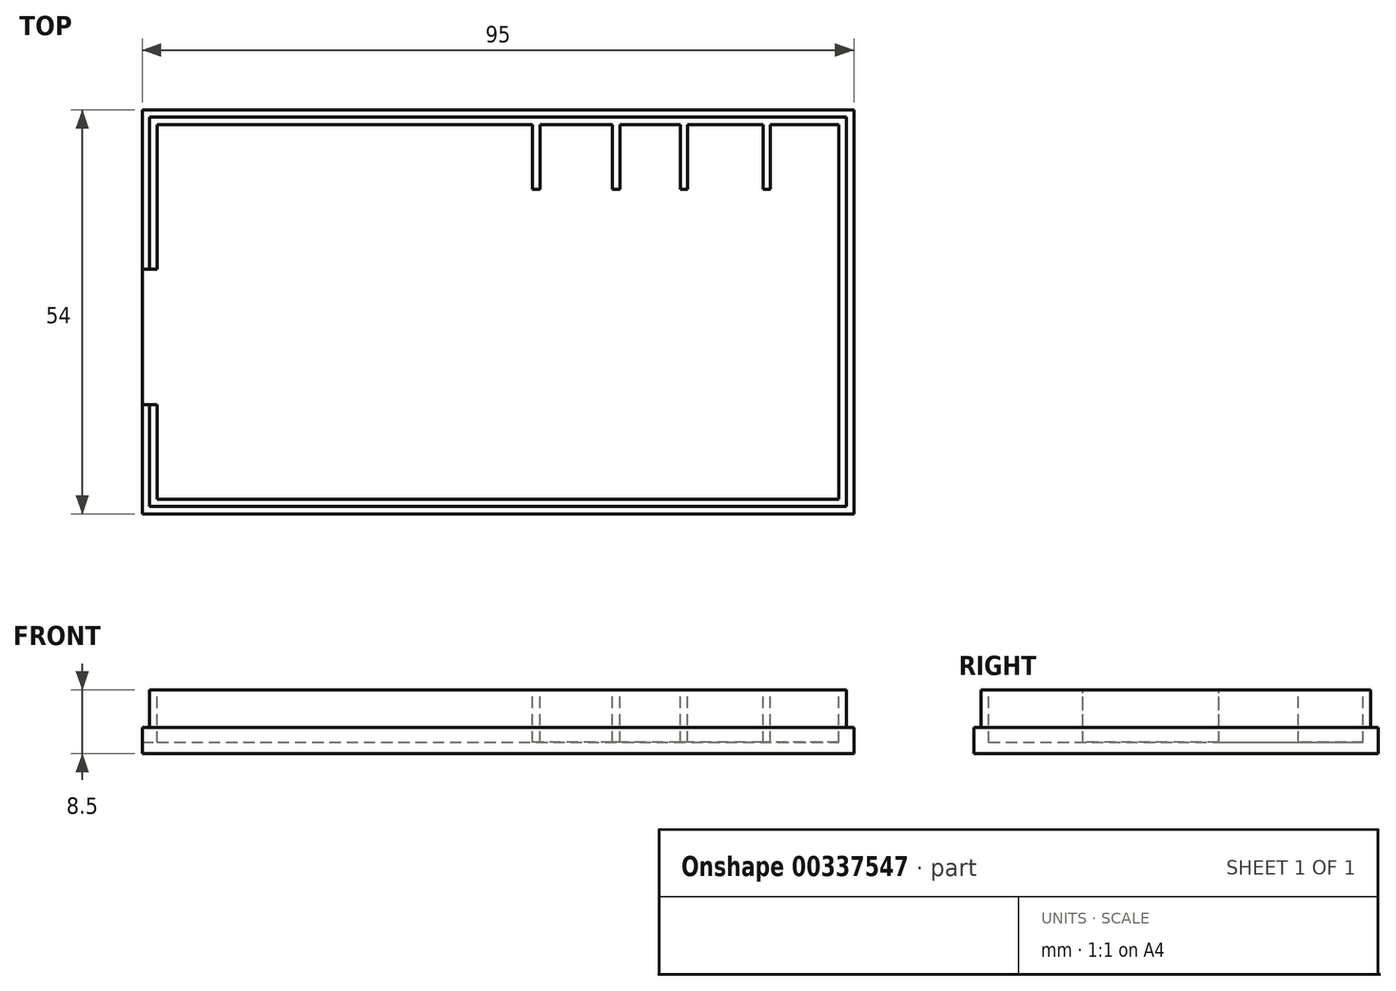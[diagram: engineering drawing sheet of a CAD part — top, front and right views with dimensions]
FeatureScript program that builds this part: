
annotation { "Feature Type Name" : "Feature", "Feature Type Description" : "" }
export const myFeature = defineFeature(function(context is Context, id is Id, definition is map)
    precondition{}
    {
        {
            var Q0;
            Q0=qCreatedBy(makeId("Top.planeOp"),FACE);
            var sketch = newSketch(context, id + "F0", { "sketchPlane" : qUnion([Q0])});
            skLineSegment(sketch, "E0.bottom", {"start": v(-47.5, 27) * mm, "end": v(47.5, 27) * mm});
            skLineSegment(sketch, "E0.top", {"start": v(-47.5, -27) * mm, "end": v(47.5, -27) * mm});
            skLineSegment(sketch, "E0.left", {"start": v(-47.5, 27) * mm, "end": v(-47.5, -27) * mm});
            skLineSegment(sketch, "E0.right", {"start": v(47.5, 27) * mm, "end": v(47.5, -27) * mm});
            skSolve(sketch);
        }
        {
            var Q0;
            Q0 = qSketchRegion(id + "F0", true);
            extrude(context, id + "F1", {"entities" : qUnion([Q0]), "depth" : 8.5 * mm});
        }
        {
            var Q0;
            Q0=makeQuery(id+"F1.opExtrude","CAP_FACE",FACE,{"disambiguationData":[OSD([sQuery(id+"F0.wireOp",EDGE,"E0.bottom"),sQuery(id+"F0.wireOp",EDGE,"E0.top"),sQuery(id+"F0.wireOp",EDGE,"E0.left"),sQuery(id+"F0.wireOp",EDGE,"E0.right")])],"isStart":false});
            var sketch = newSketch(context, id + "F2", { "sketchPlane" : qUnion([Q0])});
            skLineSegment(sketch, "E1.bottom", {"start": v(-45.5, -25) * mm, "end": v(45.5, -25) * mm});
            skLineSegment(sketch, "E1.left", {"start": v(-45.5, -25) * mm, "end": v(-45.5, 25) * mm});
            skLineSegment(sketch, "E1.right", {"start": v(45.5, -25) * mm, "end": v(45.5, 25) * mm});
            skLineSegment(sketch, "E2", {"start": v(36.37, 25) * mm, "end": v(36.37, 16.35) * mm});
            skLineSegment(sketch, "E3", {"start": v(36.37, 16.35) * mm, "end": v(35.37, 16.35) * mm});
            skLineSegment(sketch, "E4", {"start": v(35.37, 16.35) * mm, "end": v(35.37, 25) * mm});
            skLineSegment(sketch, "E5", {"start": v(45.5, 25) * mm, "end": v(36.37, 25) * mm});
            skLineSegment(sketch, "E6", {"start": v(35.37, 25) * mm, "end": v(25.32, 25) * mm});
            skLineSegment(sketch, "E7", {"start": v(25.32, 25) * mm, "end": v(25.32, 16.35) * mm});
            skLineSegment(sketch, "E8", {"start": v(25.32, 16.35) * mm, "end": v(24.32, 16.35) * mm});
            skLineSegment(sketch, "E9", {"start": v(24.32, 16.35) * mm, "end": v(24.32, 25) * mm});
            skLineSegment(sketch, "E10", {"start": v(24.32, 25) * mm, "end": v(16.26, 25) * mm});
            skLineSegment(sketch, "E11", {"start": v(16.26, 25) * mm, "end": v(16.26, 16.35) * mm});
            skLineSegment(sketch, "E12", {"start": v(16.26, 16.35) * mm, "end": v(15.26, 16.35) * mm});
            skLineSegment(sketch, "E13", {"start": v(15.26, 16.35) * mm, "end": v(15.26, 25) * mm});
            skLineSegment(sketch, "E14", {"start": v(15.26, 25) * mm, "end": v(5.62, 25) * mm});
            skLineSegment(sketch, "E15", {"start": v(5.62, 25) * mm, "end": v(5.62, 16.35) * mm});
            skLineSegment(sketch, "E16", {"start": v(5.62, 16.35) * mm, "end": v(4.62, 16.35) * mm});
            skLineSegment(sketch, "E17", {"start": v(4.62, 16.35) * mm, "end": v(4.62, 25) * mm});
            skLineSegment(sketch, "E18", {"start": v(-45.5, 25) * mm, "end": v(4.62, 25) * mm});
            skSolve(sketch);
        }
        {
            var Q0;
            Q0 = qSketchRegion(id + "F2", true);
            extrude(context, id + "F3", {"entities" : qUnion([Q0]), "operationType" : NewBodyOperationType.REMOVE, "oppositeDirection" : true, "depth" : 7 * mm});
        }
        {
            var Q0;
            Q0=makeQuery(id+"F1.opExtrude","CAP_FACE",FACE,{"disambiguationData":[OSD([sQuery(id+"F0.wireOp",EDGE,"E0.bottom"),sQuery(id+"F0.wireOp",EDGE,"E0.top"),sQuery(id+"F0.wireOp",EDGE,"E0.left"),sQuery(id+"F0.wireOp",EDGE,"E0.right")])],"isStart":false});
            var sketch = newSketch(context, id + "F4", { "sketchPlane" : qUnion([Q0])});
            skLineSegment(sketch, "E19.bottom", {"start": v(-47.5, -12.4) * mm, "end": v(-45.5, -12.4) * mm});
            skLineSegment(sketch, "E19.top", {"start": v(-47.5, 5.7) * mm, "end": v(-45.5, 5.7) * mm});
            skLineSegment(sketch, "E19.left", {"start": v(-47.5, -12.4) * mm, "end": v(-47.5, 5.7) * mm});
            skLineSegment(sketch, "E19.right", {"start": v(-45.5, -12.4) * mm, "end": v(-45.5, 5.7) * mm});
            skSolve(sketch);
        }
        {
            var Q0;
            Q0 = qSketchRegion(id + "F4", true);
            extrude(context, id + "F5", {"entities" : qUnion([Q0]), "operationType" : NewBodyOperationType.REMOVE, "oppositeDirection" : true, "depth" : 7 * mm});
        }
        {
            var Q0;
            Q0=makeQuery(id+"F1.opExtrude","CAP_FACE",FACE,{"disambiguationData":[OSD([sQuery(id+"F0.wireOp",EDGE,"E0.bottom"),sQuery(id+"F0.wireOp",EDGE,"E0.top"),sQuery(id+"F0.wireOp",EDGE,"E0.left"),sQuery(id+"F0.wireOp",EDGE,"E0.right")])],"isStart":false});
            var sketch = newSketch(context, id + "F6", { "sketchPlane" : qUnion([Q0])});
            skLineSegment(sketch, "E20", {"start": v(-46.5, -26) * mm, "end": v(46.5, -26) * mm});
            skLineSegment(sketch, "E21", {"start": v(46.5, -26) * mm, "end": v(46.5, 26) * mm});
            skLineSegment(sketch, "E22", {"start": v(46.5, 26) * mm, "end": v(-46.5, 26) * mm});
            skLineSegment(sketch, "E23", {"start": v(-46.5, 26) * mm, "end": v(-46.5, 5.7) * mm});
            skLineSegment(sketch, "E24", {"start": v(-46.5, 5.7) * mm, "end": v(-47.5, 5.7) * mm});
            skLineSegment(sketch, "E25", {"start": v(-47.5, 5.7) * mm, "end": v(-47.5, 27) * mm});
            skLineSegment(sketch, "E26", {"start": v(-47.5, 27) * mm, "end": v(47.5, 27) * mm});
            skLineSegment(sketch, "E27", {"start": v(47.5, 27) * mm, "end": v(47.5, -27) * mm});
            skLineSegment(sketch, "E28", {"start": v(47.5, -27) * mm, "end": v(-47.5, -27) * mm});
            skLineSegment(sketch, "E29", {"start": v(-47.5, -27) * mm, "end": v(-47.5, -12.4) * mm});
            skLineSegment(sketch, "E30", {"start": v(-47.5, -12.4) * mm, "end": v(-46.5, -12.4) * mm});
            skLineSegment(sketch, "E31", {"start": v(-46.5, -12.4) * mm, "end": v(-46.5, -26) * mm});
            skSolve(sketch);
        }
        {
            var Q0;
            Q0 = qSketchRegion(id + "F6", true);
            extrude(context, id + "F7", {"entities" : qUnion([Q0]), "operationType" : NewBodyOperationType.REMOVE, "oppositeDirection" : true, "depth" : 5 * mm});
        }
    });
